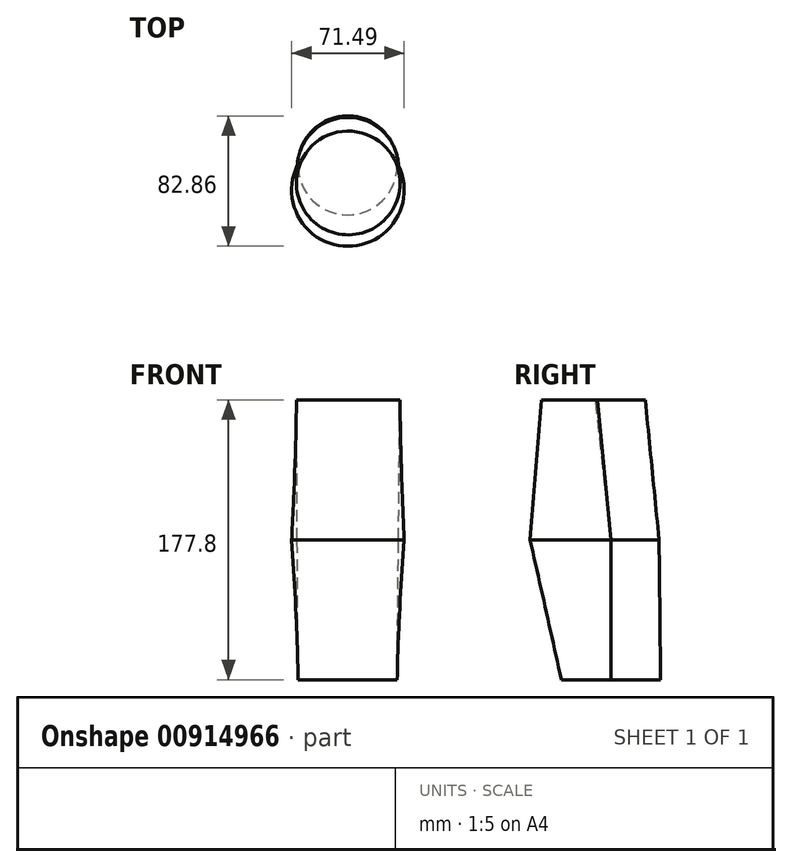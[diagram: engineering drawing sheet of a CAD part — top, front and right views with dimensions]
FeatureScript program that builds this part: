
annotation { "Feature Type Name" : "Feature", "Feature Type Description" : "" }
export const myFeature = defineFeature(function(context is Context, id is Id, definition is map)
    precondition{}
    {
        {
            var Q0;
            Q0=qCreatedBy(makeId("Top.planeOp"),FACE);
            var sketch = newSketch(context, id + "F0", { "sketchPlane" : qUnion([Q0])});
            skCircle(sketch, "E0", {"center": v(0, 0) * mm, "radius": 31.5 * mm});
            skSolve(sketch);
        }
        {
            var Q0;
            Q0=makeQuery(id+"F0.imprint","IMPRINT",FACE,{"disambiguationData":[TD([[makeQuery(id+"F0.imprint","IMPRINT",EDGE,{"derivedFrom":sQuery(id+"F0.wireOp",EDGE,"E0")}),1.0]])]});
            cPlane(context, id + "F1", {"entities" : qUnion([Q0]), "cplaneType" : CPlaneType.OFFSET, "offset" : 88.9 * mm, "width" : 152.4 * mm, "height" : 152.4 * mm});
        }
        {
            var Q0;
            Q0=qCreatedBy(id+"F1.planeOp",FACE);
            var sketch = newSketch(context, id + "F2", { "sketchPlane" : qUnion([Q0])});
            skArc(sketch, "E1", {"start": v(32.33, 0) * mm, "mid": v(0.17, 30.53) * mm, "end": v(-32, 0) * mm});
            skArc(sketch, "E2", {"start": v(-32, 0) * mm, "mid": v(0.17, -51.35) * mm, "end": v(32.33, 0) * mm});
            skSolve(sketch);
        }
        {
            var Q0;
            Q0=makeQuery(id+"F0.imprint","IMPRINT",FACE,{"disambiguationData":[TD([[makeQuery(id+"F0.imprint","IMPRINT",EDGE,{"derivedFrom":sQuery(id+"F0.wireOp",EDGE,"E0")}),1.0]])]});
            var Q1;
            Q1=makeQuery(id+"F2.imprint","IMPRINT",FACE,{"disambiguationData":[TD([[makeQuery(id+"F2.imprint","IMPRINT",EDGE,{"derivedFrom":sQuery(id+"F2.wireOp",EDGE,"E1")}),1.0]])]});
            loft(context, id + "F3", {"sheetProfilesArray" : [{ "sheetProfileEntities" : qUnion([Q0]) }, { "sheetProfileEntities" : qUnion([Q1]) }]});
        }
        {
            var Q0;
            Q0=makeQuery(id+"F2.imprint","IMPRINT",FACE,{"disambiguationData":[TD([[makeQuery(id+"F2.imprint","IMPRINT",EDGE,{"derivedFrom":sQuery(id+"F2.wireOp",EDGE,"E1")}),1.0]])]});
            cPlane(context, id + "F4", {"entities" : qUnion([Q0]), "cplaneType" : CPlaneType.OFFSET, "offset" : 88.9 * mm, "width" : 152.4 * mm, "height" : 152.4 * mm});
        }
        {
            var Q0;
            Q0=qCreatedBy(id+"F4.planeOp",FACE);
            var sketch = newSketch(context, id + "F5", { "sketchPlane" : qUnion([Q0])});
            skArc(sketch, "E3", {"start": v(33.17, -8.58) * mm, "mid": v(-0.22, 21.78) * mm, "end": v(-32.53, -9.73) * mm});
            skArc(sketch, "E4", {"start": v(-32.53, -9.73) * mm, "mid": v(0.93, -44.1) * mm, "end": v(33.17, -8.58) * mm});
            skSolve(sketch);
        }
        {
            var Q1;
            Q1=makeQuery(id+"F2.imprint","IMPRINT",FACE,{"disambiguationData":[TD([[makeQuery(id+"F2.imprint","IMPRINT",EDGE,{"derivedFrom":sQuery(id+"F2.wireOp",EDGE,"E1")}),1.0]])]});
            var Q2;
            Q2=makeQuery(id+"F5.imprint","IMPRINT",FACE,{"disambiguationData":[TD([[makeQuery(id+"F5.imprint","IMPRINT",EDGE,{"derivedFrom":sQuery(id+"F5.wireOp",EDGE,"E3")}),1.0]])]});
            loft(context, id + "F6", {"operationType" : NewBodyOperationType.ADD, "sheetProfilesArray" : [{ "sheetProfileEntities" : qUnion([Q1]) }, { "sheetProfileEntities" : qUnion([Q2]) }]});
        }
    });
